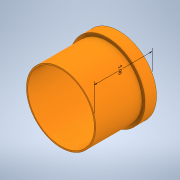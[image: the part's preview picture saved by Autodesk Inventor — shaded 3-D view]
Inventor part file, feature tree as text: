
AUTODESK INVENTOR PART (.ipt)
format: ipt  version: 2021.2 (Build 252289000, 289)  size: 134,656 bytes
history: native  units: in
note: dims shown in document units (in); Inventor stores cm internally (conversion verified against a paired STEP export)
features: extrude x5, sketch x5, other x2
ambient origin geometry x8: Origin, YZ Plane, XZ Plane, XY Plane, X Axis, Y Axis, Z Axis, Center Point
bodies: Solid1 (feature_tree)
feature tree (12):
  other  "Annotations"
  extrude  "Extrusion1"  Depth=5.75in
  extrude  "Extrusion2"  Depth=6.5in
  extrude  "Extrusion3"  Depth=1.0in TaperAngle=0.0deg
  extrude  "Extrusion4"  Depth=5.0in
  extrude  "Extrusion6"  [1 undecoded]
  sketch  "Sketch1"  dims[d2=0.0in d6=5.75in]
  sketch  "Sketch2"  dims[d7=16.0in d8=0.0in d9=6.5in]
  sketch  "Sketch3"  dims[d10=1.0in d11=0.0in d12=1.0in d13=0.0in]
  sketch  "Sketch4"  dims[d19=12.25in d20=0.0in d21=0.3706in d22=0.2703in d23=5.0in]
  sketch  "Sketch7"
  other  "Linear Dimension 1"
note: 1 required parameter value undecoded (feature->parameter linkage not recoverable at this tier; creation-order binding heuristic only, values carry confidence <= 0.55)
